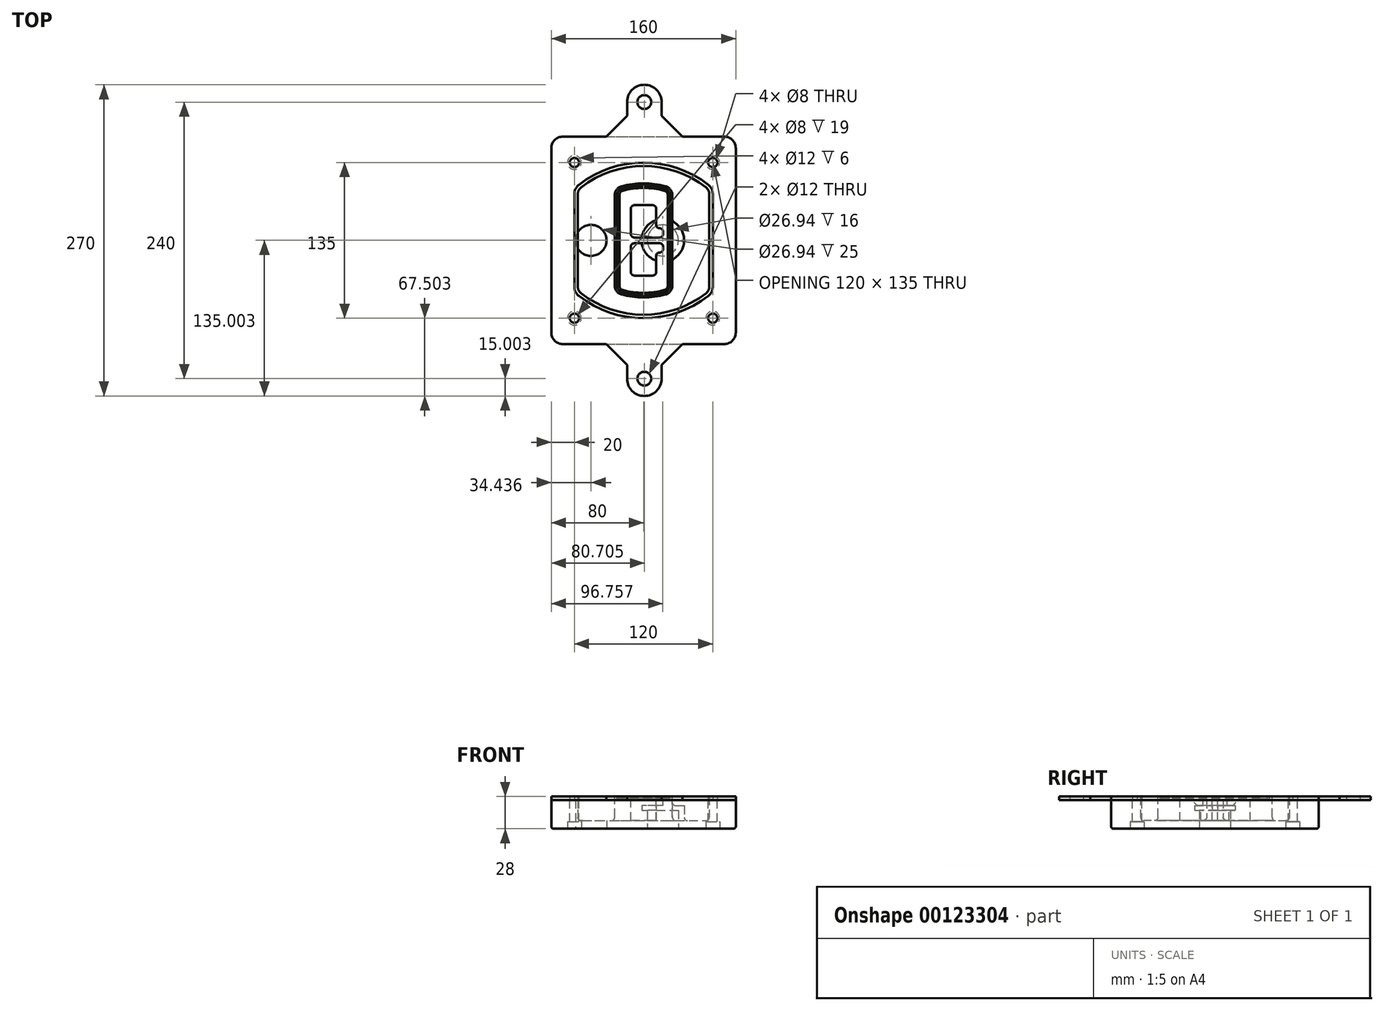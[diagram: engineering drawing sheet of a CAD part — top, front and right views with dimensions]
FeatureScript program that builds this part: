
annotation { "Feature Type Name" : "Feature", "Feature Type Description" : "" }
export const myFeature = defineFeature(function(context is Context, id is Id, definition is map)
    precondition{}
    {
        {
            var Q0;
            Q0=qCreatedBy(makeId("Top.planeOp"),FACE);
            var sketch = newSketch(context, id + "F0", { "sketchPlane" : qUnion([Q0])});
            skPoint(sketch, "E0.rect.middle", {"position": v(0, 0) * mm});
            skLineSegment(sketch, "E1.bottom", {"start": v(24.05, 28.38) * mm, "end": v(164.05, 28.38) * mm});
            skLineSegment(sketch, "E1.top", {"start": v(24.05, 208.38) * mm, "end": v(164.05, 208.38) * mm});
            skLineSegment(sketch, "E1.left", {"start": v(14.05, 38.38) * mm, "end": v(14.05, 198.38) * mm});
            skLineSegment(sketch, "E1.right", {"start": v(174.05, 38.38) * mm, "end": v(174.05, 198.38) * mm});
            skLineSegment(sketch, "E2", {"start": v(14.05, 208.38) * mm, "end": v(174.05, 28.38) * mm, "construction": true});
            skLineSegment(sketch, "E3", {"start": v(174.05, 208.38) * mm, "end": v(14.05, 28.38) * mm, "construction": true});
            skCircle(sketch, "E4", {"center": v(34.05, 185.88) * mm, "radius": 4 * mm});
            skCircle(sketch, "E5", {"center": v(154.05, 185.88) * mm, "radius": 4 * mm});
            skCircle(sketch, "E6", {"center": v(154.05, 50.88) * mm, "radius": 4 * mm});
            skCircle(sketch, "E7", {"center": v(34.05, 50.88) * mm, "radius": 4 * mm});
            skLineSegment(sketch, "E8", {"start": v(34.05, 185.88) * mm, "end": v(154.05, 185.88) * mm, "construction": true});
            skLineSegment(sketch, "E9", {"start": v(154.05, 185.88) * mm, "end": v(154.05, 50.88) * mm, "construction": true});
            skLineSegment(sketch, "E10", {"start": v(154.05, 50.88) * mm, "end": v(34.05, 50.88) * mm, "construction": true});
            skLineSegment(sketch, "E11", {"start": v(34.05, 50.88) * mm, "end": v(34.05, 185.88) * mm, "construction": true});
            skLineSegment(sketch, "E12", {"start": v(34.05, 158.68) * mm, "end": v(34.05, 78.09) * mm});
            skLineSegment(sketch, "E13", {"start": v(154.05, 158.68) * mm, "end": v(154.05, 78.09) * mm});
            skArc(sketch, "E14", {"start": v(150.2, 166.56) * mm, "mid": v(94.05, 185.88) * mm, "end": v(37.9, 166.56) * mm});
            skArc(sketch, "E15", {"start": v(37.9, 70.2) * mm, "mid": v(94.05, 50.88) * mm, "end": v(150.2, 70.2) * mm});
            skLineSegment(sketch, "E16", {"start": v(34.05, 118.38) * mm, "end": v(154.05, 118.38) * mm, "construction": true});
            skPoint(sketch, "E17.visualSharp", {"position": v(34.05, 73.38) * mm});
            skArc(sketch, "E17.filletArc", {"start": v(34.05, 78.09) * mm, "mid": v(35.06, 73.7) * mm, "end": v(37.9, 70.2) * mm});
            skPoint(sketch, "E18.visualSharp", {"position": v(34.05, 163.38) * mm});
            skArc(sketch, "E18.filletArc", {"start": v(37.9, 166.56) * mm, "mid": v(35.06, 163.06) * mm, "end": v(34.05, 158.68) * mm});
            skPoint(sketch, "E19.visualSharp", {"position": v(154.05, 163.38) * mm});
            skArc(sketch, "E19.filletArc", {"start": v(154.05, 158.68) * mm, "mid": v(153.04, 163.06) * mm, "end": v(150.2, 166.56) * mm});
            skPoint(sketch, "E20.visualSharp", {"position": v(154.05, 73.38) * mm});
            skArc(sketch, "E20.filletArc", {"start": v(150.2, 70.2) * mm, "mid": v(153.04, 73.7) * mm, "end": v(154.05, 78.09) * mm});
            skPoint(sketch, "E21.visualSharp", {"position": v(14.05, 208.38) * mm});
            skArc(sketch, "E21.filletArc", {"start": v(24.05, 208.38) * mm, "mid": v(16.98, 205.45) * mm, "end": v(14.05, 198.38) * mm});
            skPoint(sketch, "E22.visualSharp", {"position": v(174.05, 208.38) * mm});
            skArc(sketch, "E22.filletArc", {"start": v(174.05, 198.38) * mm, "mid": v(171.12, 205.45) * mm, "end": v(164.05, 208.38) * mm});
            skPoint(sketch, "E23.visualSharp", {"position": v(174.05, 28.38) * mm});
            skArc(sketch, "E23.filletArc", {"start": v(164.05, 28.38) * mm, "mid": v(171.12, 31.31) * mm, "end": v(174.05, 38.38) * mm});
            skPoint(sketch, "E24.visualSharp", {"position": v(14.05, 28.38) * mm});
            skArc(sketch, "E24.filletArc", {"start": v(14.05, 38.38) * mm, "mid": v(16.98, 31.31) * mm, "end": v(24.05, 28.38) * mm});
            skArc(sketch, "E25.0", {"start": v(151.05, 158.68) * mm, "mid": v(150.34, 161.75) * mm, "end": v(148.36, 164.2) * mm});
            skLineSegment(sketch, "E25.1", {"start": v(151.05, 158.68) * mm, "end": v(151.05, 78.09) * mm});
            skArc(sketch, "E25.2", {"start": v(148.36, 72.57) * mm, "mid": v(150.34, 75.02) * mm, "end": v(151.05, 78.09) * mm});
            skArc(sketch, "E25.3", {"start": v(39.74, 72.57) * mm, "mid": v(94.05, 53.88) * mm, "end": v(148.36, 72.57) * mm});
            skArc(sketch, "E25.4", {"start": v(37.05, 78.09) * mm, "mid": v(37.76, 75.02) * mm, "end": v(39.74, 72.57) * mm});
            skArc(sketch, "E25.5", {"start": v(148.36, 164.2) * mm, "mid": v(94.05, 182.88) * mm, "end": v(39.74, 164.2) * mm});
            skLineSegment(sketch, "E25.6", {"start": v(37.05, 158.68) * mm, "end": v(37.05, 78.09) * mm});
            skArc(sketch, "E25.7", {"start": v(39.74, 164.2) * mm, "mid": v(37.76, 161.75) * mm, "end": v(37.05, 158.68) * mm});
            skArc(sketch, "E26.0", {"start": v(35.43, 169.71) * mm, "mid": v(31.47, 164.82) * mm, "end": v(30.05, 158.68) * mm});
            skArc(sketch, "E26.1", {"start": v(152.67, 169.71) * mm, "mid": v(94.05, 189.88) * mm, "end": v(35.43, 169.71) * mm});
            skArc(sketch, "E26.2", {"start": v(158.05, 158.68) * mm, "mid": v(156.63, 164.82) * mm, "end": v(152.67, 169.71) * mm});
            skLineSegment(sketch, "E26.3", {"start": v(158.05, 158.68) * mm, "end": v(158.05, 78.09) * mm});
            skArc(sketch, "E26.4", {"start": v(152.67, 67.05) * mm, "mid": v(156.63, 71.95) * mm, "end": v(158.05, 78.09) * mm});
            skLineSegment(sketch, "E26.5", {"start": v(30.05, 158.68) * mm, "end": v(30.05, 78.09) * mm});
            skArc(sketch, "E26.6", {"start": v(35.43, 67.05) * mm, "mid": v(94.05, 46.88) * mm, "end": v(152.67, 67.05) * mm});
            skArc(sketch, "E26.7", {"start": v(30.05, 78.09) * mm, "mid": v(31.47, 71.95) * mm, "end": v(35.43, 67.05) * mm});
            skSolve(sketch);
        }
        {
            var Q0;
            Q0=makeQuery(id+"F0.imprint","IMPRINT",FACE,{"disambiguationData":[TD([[makeQuery(id+"F0.imprint","IMPRINT",EDGE,{"derivedFrom":sQuery(id+"F0.wireOp",EDGE,"E1.bottom")}),1.0]])]});
            var Q1;
            Q1=makeQuery(id+"F0.imprint","IMPRINT",FACE,{"disambiguationData":[TD([[makeQuery(id+"F0.imprint","IMPRINT",EDGE,{"derivedFrom":sQuery(id+"F0.wireOp",EDGE,"E12")}),1.0]])]});
            var Q2;
            Q2=makeQuery(id+"F0.imprint","IMPRINT",FACE,{"disambiguationData":[TD([[makeQuery(id+"F0.imprint","IMPRINT",EDGE,{"derivedFrom":sQuery(id+"F0.wireOp",EDGE,"E25.0")}),1.0]])]});
            var Q3;
            Q3=makeQuery(id+"F0.imprint","IMPRINT",FACE,{"disambiguationData":[TD([[makeQuery(id+"F0.imprint","IMPRINT",EDGE,{"derivedFrom":sQuery(id+"F0.wireOp",EDGE,"E12")}),-1.0]])]});
            extrude(context, id + "F1", {"entities" : qUnion([Q0, Q1, Q2, Q3]), "oppositeDirection" : true, "depth" : 25 * mm});
        }
        {
            var Q0;
            Q0=makeQuery(id+"F0.imprint","IMPRINT",FACE,{"disambiguationData":[TD([[makeQuery(id+"F0.imprint","IMPRINT",EDGE,{"derivedFrom":sQuery(id+"F0.wireOp",EDGE,"E12")}),1.0]])]});
            extrude(context, id + "F2", {"entities" : qUnion([Q0]), "operationType" : NewBodyOperationType.ADD, "depth" : 3 * mm});
        }
        {
            var Q0;
            Q0=makeQuery(id+"F0.imprint","IMPRINT",FACE,{"disambiguationData":[TD([[makeQuery(id+"F0.imprint","IMPRINT",EDGE,{"derivedFrom":sQuery(id+"F0.wireOp",EDGE,"E25.0")}),1.0]])]});
            extrude(context, id + "F3", {"entities" : qUnion([Q0]), "operationType" : NewBodyOperationType.REMOVE, "oppositeDirection" : true, "depth" : 18 * mm});
        }
        {
            var Q0;
            Q0=makeQuery(id+"F2.opExtrude","CAP_FACE",FACE,{"disambiguationData":[OSD([sQuery(id+"F0.wireOp",EDGE,"E12"),sQuery(id+"F0.wireOp",EDGE,"E13"),sQuery(id+"F0.wireOp",EDGE,"E14"),sQuery(id+"F0.wireOp",EDGE,"E15"),sQuery(id+"F0.wireOp",EDGE,"E17.filletArc"),sQuery(id+"F0.wireOp",EDGE,"E18.filletArc"),sQuery(id+"F0.wireOp",EDGE,"E19.filletArc"),sQuery(id+"F0.wireOp",EDGE,"E20.filletArc"),sQuery(id+"F0.wireOp",EDGE,"E25.0"),sQuery(id+"F0.wireOp",EDGE,"E25.1"),sQuery(id+"F0.wireOp",EDGE,"E25.2"),sQuery(id+"F0.wireOp",EDGE,"E25.3"),sQuery(id+"F0.wireOp",EDGE,"E25.4"),sQuery(id+"F0.wireOp",EDGE,"E25.5"),sQuery(id+"F0.wireOp",EDGE,"E25.6"),sQuery(id+"F0.wireOp",EDGE,"E25.7")])],"isStart":false});
            var sketch = newSketch(context, id + "F4", { "sketchPlane" : qUnion([Q0])});
            skArc(sketch, "E27.0", {"start": v(74.97, 71.41) * mm, "mid": v(94.05, 68.88) * mm, "end": v(113.13, 71.41) * mm});
            skArc(sketch, "E28.0", {"start": v(113.13, 165.35) * mm, "mid": v(94.05, 167.88) * mm, "end": v(74.97, 165.35) * mm});
            skLineSegment(sketch, "E29", {"start": v(69.05, 157.63) * mm, "end": v(69.05, 79.14) * mm});
            skLineSegment(sketch, "E30", {"start": v(119.05, 157.63) * mm, "end": v(119.05, 79.14) * mm});
            skLineSegment(sketch, "E31", {"start": v(69.05, 163.48) * mm, "end": v(119.05, 163.48) * mm, "construction": true});
            skLineSegment(sketch, "E32", {"start": v(69.05, 73.28) * mm, "end": v(119.05, 73.28) * mm, "construction": true});
            skPoint(sketch, "E33.visualSharp", {"position": v(69.05, 163.48) * mm});
            skArc(sketch, "E33.filletArc", {"start": v(74.97, 165.35) * mm, "mid": v(70.7, 162.5) * mm, "end": v(69.05, 157.63) * mm});
            skPoint(sketch, "E34.visualSharp", {"position": v(119.05, 163.48) * mm});
            skArc(sketch, "E34.filletArc", {"start": v(119.05, 157.63) * mm, "mid": v(117.4, 162.5) * mm, "end": v(113.13, 165.35) * mm});
            skPoint(sketch, "E35.visualSharp", {"position": v(119.05, 73.28) * mm});
            skArc(sketch, "E35.filletArc", {"start": v(113.13, 71.41) * mm, "mid": v(117.4, 74.27) * mm, "end": v(119.05, 79.14) * mm});
            skPoint(sketch, "E36.visualSharp", {"position": v(69.05, 73.28) * mm});
            skArc(sketch, "E36.filletArc", {"start": v(69.05, 79.14) * mm, "mid": v(70.7, 74.27) * mm, "end": v(74.97, 71.41) * mm});
            skArc(sketch, "E37.0", {"start": v(148.36, 164.2) * mm, "mid": v(94.05, 182.88) * mm, "end": v(39.74, 164.2) * mm});
            skArc(sketch, "E37.1", {"start": v(39.74, 164.2) * mm, "mid": v(37.76, 161.75) * mm, "end": v(37.05, 158.68) * mm});
            skLineSegment(sketch, "E37.2", {"start": v(37.05, 158.68) * mm, "end": v(37.05, 78.09) * mm});
            skArc(sketch, "E37.3", {"start": v(37.05, 78.09) * mm, "mid": v(37.76, 75.02) * mm, "end": v(39.74, 72.57) * mm});
            skArc(sketch, "E37.4", {"start": v(39.74, 72.57) * mm, "mid": v(94.05, 53.88) * mm, "end": v(148.36, 72.57) * mm});
            skArc(sketch, "E37.5", {"start": v(148.36, 72.57) * mm, "mid": v(150.34, 75.02) * mm, "end": v(151.05, 78.09) * mm});
            skLineSegment(sketch, "E37.6", {"start": v(151.05, 158.68) * mm, "end": v(151.05, 78.09) * mm});
            skArc(sketch, "E37.7", {"start": v(151.05, 158.68) * mm, "mid": v(150.34, 161.75) * mm, "end": v(148.36, 164.2) * mm});
            skLineSegment(sketch, "E38.0", {"start": v(117.05, 157.63) * mm, "end": v(117.05, 79.14) * mm});
            skArc(sketch, "E38.1", {"start": v(112.61, 73.34) * mm, "mid": v(115.81, 75.49) * mm, "end": v(117.05, 79.14) * mm});
            skArc(sketch, "E38.2", {"start": v(75.49, 73.34) * mm, "mid": v(94.05, 70.88) * mm, "end": v(112.61, 73.34) * mm});
            skArc(sketch, "E38.3", {"start": v(71.05, 79.14) * mm, "mid": v(72.29, 75.49) * mm, "end": v(75.49, 73.34) * mm});
            skLineSegment(sketch, "E38.4", {"start": v(71.05, 157.63) * mm, "end": v(71.05, 79.14) * mm});
            skArc(sketch, "E38.5", {"start": v(117.05, 157.63) * mm, "mid": v(115.81, 161.28) * mm, "end": v(112.61, 163.42) * mm});
            skArc(sketch, "E38.6", {"start": v(75.49, 163.42) * mm, "mid": v(72.29, 161.28) * mm, "end": v(71.05, 157.63) * mm});
            skArc(sketch, "E38.7", {"start": v(112.61, 163.42) * mm, "mid": v(94.05, 165.88) * mm, "end": v(75.49, 163.42) * mm});
            skArc(sketch, "E39.0", {"start": v(115.05, 157.63) * mm, "mid": v(114.23, 160.06) * mm, "end": v(112.1, 161.5) * mm});
            skLineSegment(sketch, "E39.1", {"start": v(115.05, 157.63) * mm, "end": v(115.05, 79.14) * mm});
            skArc(sketch, "E39.2", {"start": v(112.1, 75.27) * mm, "mid": v(114.23, 76.7) * mm, "end": v(115.05, 79.14) * mm});
            skArc(sketch, "E39.3", {"start": v(76, 75.27) * mm, "mid": v(94.05, 72.88) * mm, "end": v(112.1, 75.27) * mm});
            skArc(sketch, "E39.4", {"start": v(73.05, 79.14) * mm, "mid": v(73.87, 76.7) * mm, "end": v(76, 75.27) * mm});
            skArc(sketch, "E39.5", {"start": v(112.1, 161.5) * mm, "mid": v(94.05, 163.88) * mm, "end": v(76, 161.5) * mm});
            skLineSegment(sketch, "E39.6", {"start": v(73.05, 157.63) * mm, "end": v(73.05, 79.14) * mm});
            skArc(sketch, "E39.7", {"start": v(76, 161.5) * mm, "mid": v(73.87, 160.06) * mm, "end": v(73.05, 157.63) * mm});
            skLineSegment(sketch, "E40", {"start": v(69.05, 118.38) * mm, "end": v(119.05, 118.38) * mm, "construction": true});
            skLineSegment(sketch, "E41", {"start": v(83.05, 123.88) * mm, "end": v(83.05, 145.88) * mm});
            skLineSegment(sketch, "E42", {"start": v(86.05, 148.88) * mm, "end": v(102.05, 148.88) * mm});
            skLineSegment(sketch, "E43", {"start": v(105.05, 145.88) * mm, "end": v(105.05, 131.88) * mm});
            skLineSegment(sketch, "E44", {"start": v(108.05, 128.88) * mm, "end": v(108.05, 128.88) * mm});
            skLineSegment(sketch, "E45", {"start": v(111.05, 125.88) * mm, "end": v(111.05, 123.88) * mm});
            skLineSegment(sketch, "E46", {"start": v(108.05, 120.88) * mm, "end": v(86.05, 120.88) * mm});
            skPoint(sketch, "E47.visualSharp", {"position": v(83.05, 148.88) * mm});
            skArc(sketch, "E47.filletArc", {"start": v(86.05, 148.88) * mm, "mid": v(83.93, 148) * mm, "end": v(83.05, 145.88) * mm});
            skPoint(sketch, "E48.visualSharp", {"position": v(105.05, 148.88) * mm});
            skArc(sketch, "E48.filletArc", {"start": v(105.05, 145.88) * mm, "mid": v(104.17, 148) * mm, "end": v(102.05, 148.88) * mm});
            skPoint(sketch, "E49.visualSharp", {"position": v(105.05, 128.88) * mm});
            skArc(sketch, "E49.filletArc", {"start": v(105.05, 131.88) * mm, "mid": v(105.93, 129.76) * mm, "end": v(108.05, 128.88) * mm});
            skPoint(sketch, "E50.visualSharp", {"position": v(111.05, 128.88) * mm});
            skArc(sketch, "E50.filletArc", {"start": v(111.05, 125.88) * mm, "mid": v(110.17, 128) * mm, "end": v(108.05, 128.88) * mm});
            skPoint(sketch, "E51.visualSharp", {"position": v(111.05, 120.88) * mm});
            skArc(sketch, "E51.filletArc", {"start": v(108.05, 120.88) * mm, "mid": v(110.17, 121.76) * mm, "end": v(111.05, 123.88) * mm});
            skPoint(sketch, "E52.visualSharp", {"position": v(83.05, 120.88) * mm});
            skArc(sketch, "E52.filletArc", {"start": v(83.05, 123.88) * mm, "mid": v(83.93, 121.76) * mm, "end": v(86.05, 120.88) * mm});
            skLineSegment(sketch, "E53.0.MirrorCS", {"start": v(108.05, 115.88) * mm, "end": v(86.05, 115.88) * mm});
            skArc(sketch, "E54.0.MirrorCS", {"start": v(83.05, 112.88) * mm, "mid": v(83.93, 115) * mm, "end": v(86.05, 115.88) * mm});
            skLineSegment(sketch, "E55.0.MirrorCS", {"start": v(83.05, 112.88) * mm, "end": v(83.05, 90.88) * mm});
            skArc(sketch, "E56.0.MirrorCS", {"start": v(86.05, 87.88) * mm, "mid": v(83.93, 88.76) * mm, "end": v(83.05, 90.88) * mm});
            skLineSegment(sketch, "E57.0.MirrorCS", {"start": v(86.05, 87.88) * mm, "end": v(102.05, 87.88) * mm});
            skArc(sketch, "E58.0.MirrorCS", {"start": v(105.05, 90.88) * mm, "mid": v(104.17, 88.76) * mm, "end": v(102.05, 87.88) * mm});
            skLineSegment(sketch, "E59.0.MirrorCS", {"start": v(105.05, 90.88) * mm, "end": v(105.05, 104.88) * mm});
            skArc(sketch, "E60.0.MirrorCS", {"start": v(105.05, 104.88) * mm, "mid": v(105.93, 107) * mm, "end": v(108.05, 107.88) * mm});
            skArc(sketch, "E61.0.MirrorCS", {"start": v(111.05, 110.88) * mm, "mid": v(110.17, 108.76) * mm, "end": v(108.05, 107.88) * mm});
            skLineSegment(sketch, "E62.0.MirrorCS", {"start": v(111.05, 110.88) * mm, "end": v(111.05, 112.88) * mm});
            skArc(sketch, "E63.0.MirrorCS", {"start": v(108.05, 115.88) * mm, "mid": v(110.17, 115) * mm, "end": v(111.05, 112.88) * mm});
            skSolve(sketch);
        }
        {
            var Q0;
            Q0=makeQuery(id+"F4.imprint","IMPRINT",FACE,{"disambiguationData":[TD([[makeQuery(id+"F4.imprint","IMPRINT",EDGE,{"derivedFrom":sQuery(id+"F4.wireOp",EDGE,"E27.0")}),1.0]])]});
            var Q1;
            Q1=makeQuery(id+"F4.imprint","IMPRINT",FACE,{"disambiguationData":[TD([[makeQuery(id+"F4.imprint","IMPRINT",EDGE,{"derivedFrom":sQuery(id+"F4.wireOp",EDGE,"E38.0")}),-1.0]])]});
            var Q2;
            Q2=makeQuery(id+"F4.imprint","IMPRINT",FACE,{"disambiguationData":[TD([[makeQuery(id+"F4.imprint","IMPRINT",EDGE,{"derivedFrom":sQuery(id+"F4.wireOp",EDGE,"E39.0")}),1.0]])]});
            extrude(context, id + "F5", {"entities" : qUnion([Q0, Q1, Q2]), "operationType" : NewBodyOperationType.ADD, "endBound" : BoundingType.UP_TO_NEXT, "oppositeDirection" : true, "depth" : 25 * mm});
        }
        {
            var Q0;
            Q0=makeQuery(id+"F4.imprint","IMPRINT",FACE,{"disambiguationData":[TD([[makeQuery(id+"F4.imprint","IMPRINT",EDGE,{"derivedFrom":sQuery(id+"F4.wireOp",EDGE,"E38.0")}),-1.0]])]});
            extrude(context, id + "F6", {"entities" : qUnion([Q0]), "operationType" : NewBodyOperationType.REMOVE, "oppositeDirection" : true, "depth" : 2 * mm});
        }
        {
            var Q0;
            Q0=makeQuery(id+"F1.opExtrude","CAP_FACE",FACE,{"disambiguationData":[OSD([sQuery(id+"F0.wireOp",EDGE,"E1.bottom"),sQuery(id+"F0.wireOp",EDGE,"E1.top"),sQuery(id+"F0.wireOp",EDGE,"E1.left"),sQuery(id+"F0.wireOp",EDGE,"E1.right"),sQuery(id+"F0.wireOp",EDGE,"E4"),sQuery(id+"F0.wireOp",EDGE,"E5"),sQuery(id+"F0.wireOp",EDGE,"E6"),sQuery(id+"F0.wireOp",EDGE,"E7"),sQuery(id+"F0.wireOp",EDGE,"E21.filletArc"),sQuery(id+"F0.wireOp",EDGE,"E22.filletArc"),sQuery(id+"F0.wireOp",EDGE,"E23.filletArc"),sQuery(id+"F0.wireOp",EDGE,"E24.filletArc")])],"isStart":false});
            var sketch = newSketch(context, id + "F7", { "sketchPlane" : qUnion([Q0])});
            skCircle(sketch, "E64", {"center": v(110.8, -118.38) * mm, "radius": 13.47 * mm});
            skCircle(sketch, "E65", {"center": v(48.49, -118.38) * mm, "radius": 13.47 * mm});
            skLineSegment(sketch, "E66", {"start": v(174.05, -118.38) * mm, "end": v(14.05, -118.38) * mm});
            skCircle(sketch, "E67", {"center": v(110.8, -118.38) * mm, "radius": 18.47 * mm});
            skCircle(sketch, "E68", {"center": v(154.05, -185.88) * mm, "radius": 6 * mm});
            skCircle(sketch, "E69", {"center": v(34.05, -185.88) * mm, "radius": 6 * mm});
            skCircle(sketch, "E70", {"center": v(34.05, -50.88) * mm, "radius": 6 * mm});
            skCircle(sketch, "E71", {"center": v(154.05, -50.88) * mm, "radius": 6 * mm});
            skSolve(sketch);
        }
        {
            var Q0;
            {var subQ1=sQuery(id+"F7.wireOp",EDGE,"E66");var subQ4=sQuery(id+"F7.wireOp",EDGE,"E64");var subQ6=makeQuery(id+"F7.imprint","INTERSECT",VERTEX,{"disambiguationData":[OD(0.0)],"derivedFrom":[subQ4,subQ1]});Q0=makeQuery(id+"F7.imprint","IMPRINT",FACE,{"disambiguationData":[TD([[makeQuery(id+"F7.imprint","IMPRINT",EDGE,{"disambiguationData":[TD([[subQ6,-1.0]])],"derivedFrom":subQ4}),-1.0]])]});}
            var Q1;
            {var subQ0=sQuery(id+"F7.wireOp",EDGE,"E66");var subQ1=sQuery(id+"F7.wireOp",EDGE,"E64");var subQ3=makeQuery(id+"F7.imprint","INTERSECT",VERTEX,{"disambiguationData":[OD(0.0)],"derivedFrom":[subQ1,subQ0]});Q1=makeQuery(id+"F7.imprint","IMPRINT",FACE,{"disambiguationData":[TD([[makeQuery(id+"F7.imprint","IMPRINT",EDGE,{"disambiguationData":[TD([[subQ3,-1.0]])],"derivedFrom":subQ1}),1.0]])]});}
            var Q2;
            {var subQ0=sQuery(id+"F7.wireOp",EDGE,"E66");var subQ1=sQuery(id+"F7.wireOp",EDGE,"E64");var subQ3=makeQuery(id+"F7.imprint","INTERSECT",VERTEX,{"disambiguationData":[OD(0.0)],"derivedFrom":[subQ1,subQ0]});Q2=makeQuery(id+"F7.imprint","IMPRINT",FACE,{"disambiguationData":[TD([[makeQuery(id+"F7.imprint","IMPRINT",EDGE,{"disambiguationData":[TD([[subQ3,1.0]])],"derivedFrom":subQ1}),1.0]])]});}
            var Q3;
            {var subQ1=sQuery(id+"F7.wireOp",EDGE,"E66");var subQ4=sQuery(id+"F7.wireOp",EDGE,"E64");var subQ6=makeQuery(id+"F7.imprint","INTERSECT",VERTEX,{"disambiguationData":[OD(0.0)],"derivedFrom":[subQ4,subQ1]});Q3=makeQuery(id+"F7.imprint","IMPRINT",FACE,{"disambiguationData":[TD([[makeQuery(id+"F7.imprint","IMPRINT",EDGE,{"disambiguationData":[TD([[subQ6,1.0]])],"derivedFrom":subQ4}),-1.0]])]});}
            extrude(context, id + "F8", {"entities" : qUnion([Q0, Q1, Q2, Q3]), "operationType" : NewBodyOperationType.ADD, "oppositeDirection" : true, "depth" : 20 * mm});
        }
        {
            var Q0;
            {var subQ0=sQuery(id+"F7.wireOp",EDGE,"E66");var subQ1=sQuery(id+"F7.wireOp",EDGE,"E64");var subQ3=makeQuery(id+"F7.imprint","INTERSECT",VERTEX,{"disambiguationData":[OD(0.0)],"derivedFrom":[subQ1,subQ0]});Q0=makeQuery(id+"F7.imprint","IMPRINT",FACE,{"disambiguationData":[TD([[makeQuery(id+"F7.imprint","IMPRINT",EDGE,{"disambiguationData":[TD([[subQ3,-1.0]])],"derivedFrom":subQ1}),1.0]])]});}
            var Q1;
            {var subQ0=sQuery(id+"F7.wireOp",EDGE,"E66");var subQ1=sQuery(id+"F7.wireOp",EDGE,"E64");var subQ3=makeQuery(id+"F7.imprint","INTERSECT",VERTEX,{"disambiguationData":[OD(0.0)],"derivedFrom":[subQ1,subQ0]});Q1=makeQuery(id+"F7.imprint","IMPRINT",FACE,{"disambiguationData":[TD([[makeQuery(id+"F7.imprint","IMPRINT",EDGE,{"disambiguationData":[TD([[subQ3,1.0]])],"derivedFrom":subQ1}),1.0]])]});}
            extrude(context, id + "F9", {"entities" : qUnion([Q0, Q1]), "operationType" : NewBodyOperationType.REMOVE, "oppositeDirection" : true, "depth" : 16 * mm});
        }
        {
            var Q0;
            {var subQ0=sQuery(id+"F7.wireOp",EDGE,"E66");var subQ1=sQuery(id+"F7.wireOp",EDGE,"E65");var subQ3=makeQuery(id+"F7.imprint","INTERSECT",VERTEX,{"disambiguationData":[OD(0.0)],"derivedFrom":[subQ1,subQ0]});Q0=makeQuery(id+"F7.imprint","IMPRINT",FACE,{"disambiguationData":[TD([[makeQuery(id+"F7.imprint","IMPRINT",EDGE,{"disambiguationData":[TD([[subQ3,-1.0]])],"derivedFrom":subQ1}),1.0]])]});}
            var Q1;
            {var subQ0=sQuery(id+"F7.wireOp",EDGE,"E66");var subQ1=sQuery(id+"F7.wireOp",EDGE,"E65");var subQ3=makeQuery(id+"F7.imprint","INTERSECT",VERTEX,{"disambiguationData":[OD(0.0)],"derivedFrom":[subQ1,subQ0]});Q1=makeQuery(id+"F7.imprint","IMPRINT",FACE,{"disambiguationData":[TD([[makeQuery(id+"F7.imprint","IMPRINT",EDGE,{"disambiguationData":[TD([[subQ3,1.0]])],"derivedFrom":subQ1}),1.0]])]});}
            extrude(context, id + "F10", {"entities" : qUnion([Q0, Q1]), "operationType" : NewBodyOperationType.REMOVE, "oppositeDirection" : true, "depth" : 25 * mm});
        }
        {
            var Q0;
            Q0=makeQuery(id+"F7.imprint","IMPRINT",FACE,{"disambiguationData":[TD([[makeQuery(id+"F7.imprint","IMPRINT",EDGE,{"derivedFrom":sQuery(id+"F7.wireOp",EDGE,"E68")}),1.0]])]});
            var Q1;
            Q1=makeQuery(id+"F7.imprint","IMPRINT",FACE,{"disambiguationData":[TD([[makeQuery(id+"F7.imprint","IMPRINT",EDGE,{"derivedFrom":makeQuery(id+"F1.opExtrude","CAP_EDGE",EDGE,{"disambiguationData":[OSD([sQuery(id+"F0.wireOp",EDGE,"E5")])],"isStart":false})}),-1.0]])]});
            var Q2;
            Q2=makeQuery(id+"F7.imprint","IMPRINT",FACE,{"disambiguationData":[TD([[makeQuery(id+"F7.imprint","IMPRINT",EDGE,{"derivedFrom":sQuery(id+"F7.wireOp",EDGE,"E69")}),1.0]])]});
            var Q3;
            Q3=makeQuery(id+"F7.imprint","IMPRINT",FACE,{"disambiguationData":[TD([[makeQuery(id+"F7.imprint","IMPRINT",EDGE,{"derivedFrom":makeQuery(id+"F1.opExtrude","CAP_EDGE",EDGE,{"disambiguationData":[OSD([sQuery(id+"F0.wireOp",EDGE,"E4")])],"isStart":false})}),-1.0]])]});
            var Q4;
            Q4=makeQuery(id+"F7.imprint","IMPRINT",FACE,{"disambiguationData":[TD([[makeQuery(id+"F7.imprint","IMPRINT",EDGE,{"derivedFrom":sQuery(id+"F7.wireOp",EDGE,"E70")}),1.0]])]});
            var Q5;
            Q5=makeQuery(id+"F7.imprint","IMPRINT",FACE,{"disambiguationData":[TD([[makeQuery(id+"F7.imprint","IMPRINT",EDGE,{"derivedFrom":makeQuery(id+"F1.opExtrude","CAP_EDGE",EDGE,{"disambiguationData":[OSD([sQuery(id+"F0.wireOp",EDGE,"E7")])],"isStart":false})}),-1.0]])]});
            var Q6;
            Q6=makeQuery(id+"F7.imprint","IMPRINT",FACE,{"disambiguationData":[TD([[makeQuery(id+"F7.imprint","IMPRINT",EDGE,{"derivedFrom":sQuery(id+"F7.wireOp",EDGE,"E71")}),1.0]])]});
            var Q7;
            Q7=makeQuery(id+"F7.imprint","IMPRINT",FACE,{"disambiguationData":[TD([[makeQuery(id+"F7.imprint","IMPRINT",EDGE,{"derivedFrom":makeQuery(id+"F1.opExtrude","CAP_EDGE",EDGE,{"disambiguationData":[OSD([sQuery(id+"F0.wireOp",EDGE,"E6")])],"isStart":false})}),-1.0]])]});
            extrude(context, id + "F11", {"entities" : qUnion([Q0, Q1, Q2, Q3, Q4, Q5, Q6, Q7]), "operationType" : NewBodyOperationType.REMOVE, "oppositeDirection" : true, "depth" : 6 * mm});
        }
        {
            var Q0;
            Q0=makeQuery(id+"F9.boolean.opBoolean","COPY",FACE,{"derivedFrom":makeQuery(id+"F9.opExtrude","CAP_FACE",FACE,{"disambiguationData":[OSD([sQuery(id+"F7.wireOp",EDGE,"E64")])],"isStart":false})});
            var sketch = newSketch(context, id + "F12", { "sketchPlane" : qUnion([Q0])});
            skArc(sketch, "E72.0", {"start": v(105.05, -100.83) * mm, "mid": v(96.62, -106.56) * mm, "end": v(92.5, -115.88) * mm});
            skArc(sketch, "E72.1", {"start": v(92.5, -120.88) * mm, "mid": v(96.62, -130.2) * mm, "end": v(105.05, -135.93) * mm});
            skLineSegment(sketch, "E73", {"start": v(92.5, -120.88) * mm, "end": v(108.05, -120.88) * mm});
            skLineSegment(sketch, "E74.0", {"start": v(108.05, -115.88) * mm, "end": v(92.5, -115.88) * mm});
            skArc(sketch, "E74.1", {"start": v(108.05, -115.88) * mm, "mid": v(110.17, -115) * mm, "end": v(111.05, -112.88) * mm});
            skLineSegment(sketch, "E74.2", {"start": v(111.05, -110.88) * mm, "end": v(111.05, -112.88) * mm});
            skArc(sketch, "E74.3", {"start": v(111.05, -110.88) * mm, "mid": v(110.17, -108.76) * mm, "end": v(108.05, -107.88) * mm});
            skArc(sketch, "E74.4", {"start": v(105.05, -104.88) * mm, "mid": v(105.93, -107) * mm, "end": v(108.05, -107.88) * mm});
            skLineSegment(sketch, "E74.5", {"start": v(105.05, -100.83) * mm, "end": v(105.05, -104.88) * mm});
            skLineSegment(sketch, "E74.7", {"start": v(108.05, -120.88) * mm, "end": v(92.5, -120.88) * mm});
            skArc(sketch, "E74.8", {"start": v(108.05, -120.88) * mm, "mid": v(110.17, -121.76) * mm, "end": v(111.05, -123.88) * mm});
            skLineSegment(sketch, "E74.9", {"start": v(111.05, -125.88) * mm, "end": v(111.05, -123.88) * mm});
            skArc(sketch, "E74.10", {"start": v(111.05, -125.88) * mm, "mid": v(110.17, -128) * mm, "end": v(108.05, -128.88) * mm});
            skArc(sketch, "E74.11", {"start": v(105.05, -131.88) * mm, "mid": v(105.93, -129.76) * mm, "end": v(108.05, -128.88) * mm});
            skLineSegment(sketch, "E74.12", {"start": v(105.05, -135.93) * mm, "end": v(105.05, -131.88) * mm});
            skPoint(sketch, "E75.orphan", {"position": v(105.05, -145.88) * mm});
            skPoint(sketch, "E76.orphan", {"position": v(86.05, -120.88) * mm});
            skPoint(sketch, "E77.orphan", {"position": v(86.05, -115.88) * mm});
            skPoint(sketch, "E78.orphan", {"position": v(105.05, -90.88) * mm});
            skSolve(sketch);
        }
        {
            var Q0;
            {var subQ7=sQuery(id+"F12.wireOp",EDGE,"E72.0");var subQ14=sQuery(id+"F12.wireOp",EDGE,"E72.1");var subQ16=sQuery(id+"F12.wireOp",EDGE,"E74.1");var subQ18=sQuery(id+"F12.wireOp",EDGE,"E74.8");Q0=qUnion([makeQuery(id+"F12.imprint","IMPRINT",FACE,{"disambiguationData":[TD([[makeQuery(id+"F12.imprint","IMPRINT",EDGE,{"derivedFrom":subQ7}),1.0]])]}),makeQuery(id+"F12.imprint","IMPRINT",FACE,{"disambiguationData":[TD([[makeQuery(id+"F12.imprint","IMPRINT",EDGE,{"derivedFrom":subQ14}),1.0]])]}),makeQuery(id+"F12.imprint","IMPRINT",FACE,{"disambiguationData":[TD([[makeQuery(id+"F12.imprint","IMPRINT",EDGE,{"derivedFrom":subQ16}),1.0]])]}),makeQuery(id+"F12.imprint","IMPRINT",FACE,{"disambiguationData":[TD([[makeQuery(id+"F12.imprint","IMPRINT",EDGE,{"derivedFrom":subQ18}),-1.0]])]})]);}
            var Q1;
            Q1=makeQuery(id+"F5.boolean.opBoolean","SPLIT",FACE,{"disambiguationData":[TD([makeQuery(id+"F5.opExtrude","SWEPT_FACE",FACE,{"disambiguationData":[OSD([sQuery(id+"F4.wireOp",EDGE,"E41")])]})])],"derivedFrom":makeQuery(id+"F3.boolean.opBoolean","COPY",FACE,{"derivedFrom":makeQuery(id+"F3.opExtrude","CAP_FACE",FACE,{"disambiguationData":[OSD([sQuery(id+"F0.wireOp",EDGE,"E25.0"),sQuery(id+"F0.wireOp",EDGE,"E25.1"),sQuery(id+"F0.wireOp",EDGE,"E25.2"),sQuery(id+"F0.wireOp",EDGE,"E25.3"),sQuery(id+"F0.wireOp",EDGE,"E25.4"),sQuery(id+"F0.wireOp",EDGE,"E25.5"),sQuery(id+"F0.wireOp",EDGE,"E25.6"),sQuery(id+"F0.wireOp",EDGE,"E25.7")])],"isStart":false})})});
            extrude(context, id + "F13", {"entities" : qUnion([Q0]), "operationType" : NewBodyOperationType.REMOVE, "endBound" : BoundingType.UP_TO_SURFACE, "endBoundEntityFace" : qUnion([Q1]), "depth" : 25 * mm});
        }
        {
            var Q0;
            Q0=makeQuery(id+"F3.boolean.opBoolean","COPY",EDGE,{"derivedFrom":makeQuery(id+"F3.opExtrude","CAP_EDGE",EDGE,{"disambiguationData":[OSD([sQuery(id+"F0.wireOp",EDGE,"E25.6")])],"isStart":false})});
            var Q1;
            Q1=makeQuery(id+"F8.boolean.opBoolean","INTERSECT",EDGE,{"derivedFrom":[makeQuery(id+"F5.opExtrude","SWEPT_FACE",FACE,{"disambiguationData":[OSD([sQuery(id+"F4.wireOp",EDGE,"E30")])]}),makeQuery(id+"F8.opExtrude","CAP_FACE",FACE,{"disambiguationData":[OSD([sQuery(id+"F7.wireOp",EDGE,"E67")])],"isStart":false})]});
            var Q2;
            Q2=makeQuery(id+"F8.boolean.opBoolean","INTERSECT",EDGE,{"disambiguationData":[OD(1.0)],"derivedFrom":[makeQuery(id+"F5.opExtrude","SWEPT_FACE",FACE,{"disambiguationData":[OSD([sQuery(id+"F4.wireOp",EDGE,"E30")])]}),makeQuery(id+"F8.opExtrude","SWEPT_FACE",FACE,{"disambiguationData":[OSD([sQuery(id+"F7.wireOp",EDGE,"E67")])]})]});
            var Q3;
            {var subQ0=sQuery(id+"F4.wireOp",EDGE,"E30");Q3=makeQuery(id+"F8.boolean.opBoolean","SPLIT",EDGE,{"disambiguationData":[TD([makeQuery(id+"F5.opExtrude","SWEPT_FACE",FACE,{"disambiguationData":[OSD([sQuery(id+"F4.wireOp",EDGE,"E35.filletArc")])]})])],"derivedFrom":makeQuery(id+"F5.opExtrude","CAP_EDGE",EDGE,{"disambiguationData":[OSD([subQ0])],"isStart":false})});}
            var Q4;
            {var subQ0=sQuery(id+"F0.wireOp",EDGE,"E25.7");var subQ1=sQuery(id+"F0.wireOp",EDGE,"E25.1");var subQ2=sQuery(id+"F0.wireOp",EDGE,"E25.6");var subQ3=sQuery(id+"F0.wireOp",EDGE,"E25.5");var subQ4=sQuery(id+"F0.wireOp",EDGE,"E25.4");var subQ5=sQuery(id+"F0.wireOp",EDGE,"E25.0");var subQ6=sQuery(id+"F0.wireOp",EDGE,"E25.2");var subQ7=sQuery(id+"F0.wireOp",EDGE,"E25.3");Q4=makeQuery(id+"F8.boolean.opBoolean","INTERSECT",EDGE,{"derivedFrom":[makeQuery(id+"F5.boolean.opBoolean","SPLIT",FACE,{"disambiguationData":[TD([makeQuery(id+"F2.opExtrude","SWEPT_FACE",FACE,{"disambiguationData":[OSD([subQ5])]})])],"derivedFrom":makeQuery(id+"F3.boolean.opBoolean","COPY",FACE,{"derivedFrom":makeQuery(id+"F3.opExtrude","CAP_FACE",FACE,{"disambiguationData":[OSD([subQ5,subQ1,subQ6,subQ7,subQ4,subQ3,subQ2,subQ0])],"isStart":false})})}),makeQuery(id+"F8.opExtrude","SWEPT_FACE",FACE,{"disambiguationData":[OSD([sQuery(id+"F7.wireOp",EDGE,"E67")])]})]});}
            var Q5;
            Q5=makeQuery(id+"F8.boolean.opBoolean","INTERSECT",EDGE,{"disambiguationData":[OD(0.0)],"derivedFrom":[makeQuery(id+"F5.opExtrude","SWEPT_FACE",FACE,{"disambiguationData":[OSD([sQuery(id+"F4.wireOp",EDGE,"E30")])]}),makeQuery(id+"F8.opExtrude","SWEPT_FACE",FACE,{"disambiguationData":[OSD([sQuery(id+"F7.wireOp",EDGE,"E67")])]})]});
            fillet(context, id + "F14", {"entities" : qUnion([Q0, Q1, Q2, Q3, Q4, Q5]), "radius" : 3 * mm, "tangentPropagation" : true, "allowEdgeOverflow" : false});
        }
        {
            var Q0;
            Q0=makeQuery(id+"F1.opExtrude","CAP_EDGE",EDGE,{"disambiguationData":[OSD([sQuery(id+"F0.wireOp",EDGE,"E1.bottom")])],"isStart":false});
            fillet(context, id + "F15", {"entities" : qUnion([Q0]), "radius" : 2 * mm, "tangentPropagation" : true, "allowEdgeOverflow" : false});
        }
        {
            var Q0;
            {var subQ0=sQuery(id+"F0.wireOp",EDGE,"E1.bottom");var subQ1=sQuery(id+"F0.wireOp",EDGE,"E1.top");var subQ2=sQuery(id+"F0.wireOp",EDGE,"E1.left");var subQ3=sQuery(id+"F0.wireOp",EDGE,"E1.right");var subQ4=sQuery(id+"F0.wireOp",EDGE,"E4");var subQ5=sQuery(id+"F0.wireOp",EDGE,"E5");var subQ6=sQuery(id+"F0.wireOp",EDGE,"E6");var subQ7=sQuery(id+"F0.wireOp",EDGE,"E7");var subQ8=sQuery(id+"F0.wireOp",EDGE,"E21.filletArc");var subQ9=sQuery(id+"F0.wireOp",EDGE,"E22.filletArc");var subQ10=sQuery(id+"F0.wireOp",EDGE,"E23.filletArc");var subQ11=sQuery(id+"F0.wireOp",EDGE,"E24.filletArc");Q0=makeQuery(id+"F2.boolean.opBoolean","SPLIT",FACE,{"disambiguationData":[TD([makeQuery(id+"F1.opExtrude","SWEPT_FACE",FACE,{"disambiguationData":[OSD([subQ0])]})])],"derivedFrom":makeQuery(id+"F1.opExtrude","CAP_FACE",FACE,{"disambiguationData":[OSD([subQ0,subQ1,subQ2,subQ3,subQ4,subQ5,subQ6,subQ7,subQ8,subQ9,subQ10,subQ11])],"isStart":true})});}
            var sketch = newSketch(context, id + "F16", { "sketchPlane" : qUnion([Q0])});
            skLineSegment(sketch, "E79", {"start": v(61.76, 208.38) * mm, "end": v(79.76, 226.38) * mm});
            skLineSegment(sketch, "E80", {"start": v(79.76, 226.38) * mm, "end": v(79.76, 238.38) * mm});
            skLineSegment(sketch, "E81", {"start": v(127.76, 208.38) * mm, "end": v(109.76, 226.38) * mm});
            skLineSegment(sketch, "E82", {"start": v(109.76, 226.38) * mm, "end": v(109.76, 238.38) * mm});
            skArc(sketch, "E83", {"start": v(109.76, 238.38) * mm, "mid": v(94.76, 253.38) * mm, "end": v(79.76, 238.38) * mm});
            skCircle(sketch, "E84", {"center": v(94.76, 238.38) * mm, "radius": 6 * mm});
            skLineSegment(sketch, "E85", {"start": v(94.76, 238.38) * mm, "end": v(94.76, 208.38) * mm, "construction": true});
            skLineSegment(sketch, "E86", {"start": v(14.05, 118.38) * mm, "end": v(174.05, 118.38) * mm, "construction": true});
            skLineSegment(sketch, "E87.MirrorCS", {"start": v(61.76, 28.38) * mm, "end": v(79.76, 10.38) * mm});
            skLineSegment(sketch, "E88.MirrorCS", {"start": v(79.76, 10.38) * mm, "end": v(79.76, -1.62) * mm});
            skLineSegment(sketch, "E89.MirrorCS", {"start": v(127.76, 28.38) * mm, "end": v(109.76, 10.38) * mm});
            skLineSegment(sketch, "E90.MirrorCS", {"start": v(109.76, 10.38) * mm, "end": v(109.76, -1.62) * mm});
            skCircle(sketch, "E91.MirrorC", {"center": v(94.76, -1.62) * mm, "radius": 6 * mm});
            skArc(sketch, "E92.MirrorCS", {"start": v(109.76, -1.62) * mm, "mid": v(94.76, -16.62) * mm, "end": v(79.76, -1.62) * mm});
            skLineSegment(sketch, "E93.MirrorCS", {"start": v(94.76, -1.62) * mm, "end": v(94.76, 28.38) * mm, "construction": true});
            skLineSegment(sketch, "E94", {"start": v(61.76, 208.38) * mm, "end": v(127.76, 208.38) * mm});
            skLineSegment(sketch, "E95", {"start": v(61.76, 28.38) * mm, "end": v(127.76, 28.38) * mm});
            skSolve(sketch);
        }
        {
            var Q0;
            Q0=makeQuery(id+"F16.imprint","IMPRINT",FACE,{"disambiguationData":[TD([[makeQuery(id+"F16.imprint","IMPRINT",EDGE,{"derivedFrom":sQuery(id+"F16.wireOp",EDGE,"E79")}),-1.0]])]});
            var Q1;
            Q1=makeQuery(id+"F16.imprint","IMPRINT",FACE,{"disambiguationData":[TD([[makeQuery(id+"F16.imprint","IMPRINT",EDGE,{"derivedFrom":sQuery(id+"F16.wireOp",EDGE,"E87.MirrorCS")}),1.0]])]});
            var Q2;
            {var subQ4=sQuery(id+"F16.wireOp",EDGE,"E94");Q2=makeQuery(id+"F16.imprint","IMPRINT",FACE,{"disambiguationData":[TD([[makeQuery(id+"F16.imprint","IMPRINT",EDGE,{"derivedFrom":subQ4}),-1.0]])]});}
            var Q3;
            Q3=makeQuery(id+"F2.opExtrude","CAP_FACE",FACE,{"disambiguationData":[OSD([sQuery(id+"F0.wireOp",EDGE,"E12"),sQuery(id+"F0.wireOp",EDGE,"E13"),sQuery(id+"F0.wireOp",EDGE,"E14"),sQuery(id+"F0.wireOp",EDGE,"E15"),sQuery(id+"F0.wireOp",EDGE,"E17.filletArc"),sQuery(id+"F0.wireOp",EDGE,"E18.filletArc"),sQuery(id+"F0.wireOp",EDGE,"E19.filletArc"),sQuery(id+"F0.wireOp",EDGE,"E20.filletArc"),sQuery(id+"F0.wireOp",EDGE,"E25.0"),sQuery(id+"F0.wireOp",EDGE,"E25.1"),sQuery(id+"F0.wireOp",EDGE,"E25.2"),sQuery(id+"F0.wireOp",EDGE,"E25.3"),sQuery(id+"F0.wireOp",EDGE,"E25.4"),sQuery(id+"F0.wireOp",EDGE,"E25.5"),sQuery(id+"F0.wireOp",EDGE,"E25.6"),sQuery(id+"F0.wireOp",EDGE,"E25.7")])],"isStart":false});
            extrude(context, id + "F17", {"entities" : qUnion([Q0, Q1, Q2]), "endBound" : BoundingType.UP_TO_SURFACE, "endBoundEntityFace" : qUnion([Q3]), "depth" : 25 * mm});
        }
    });
